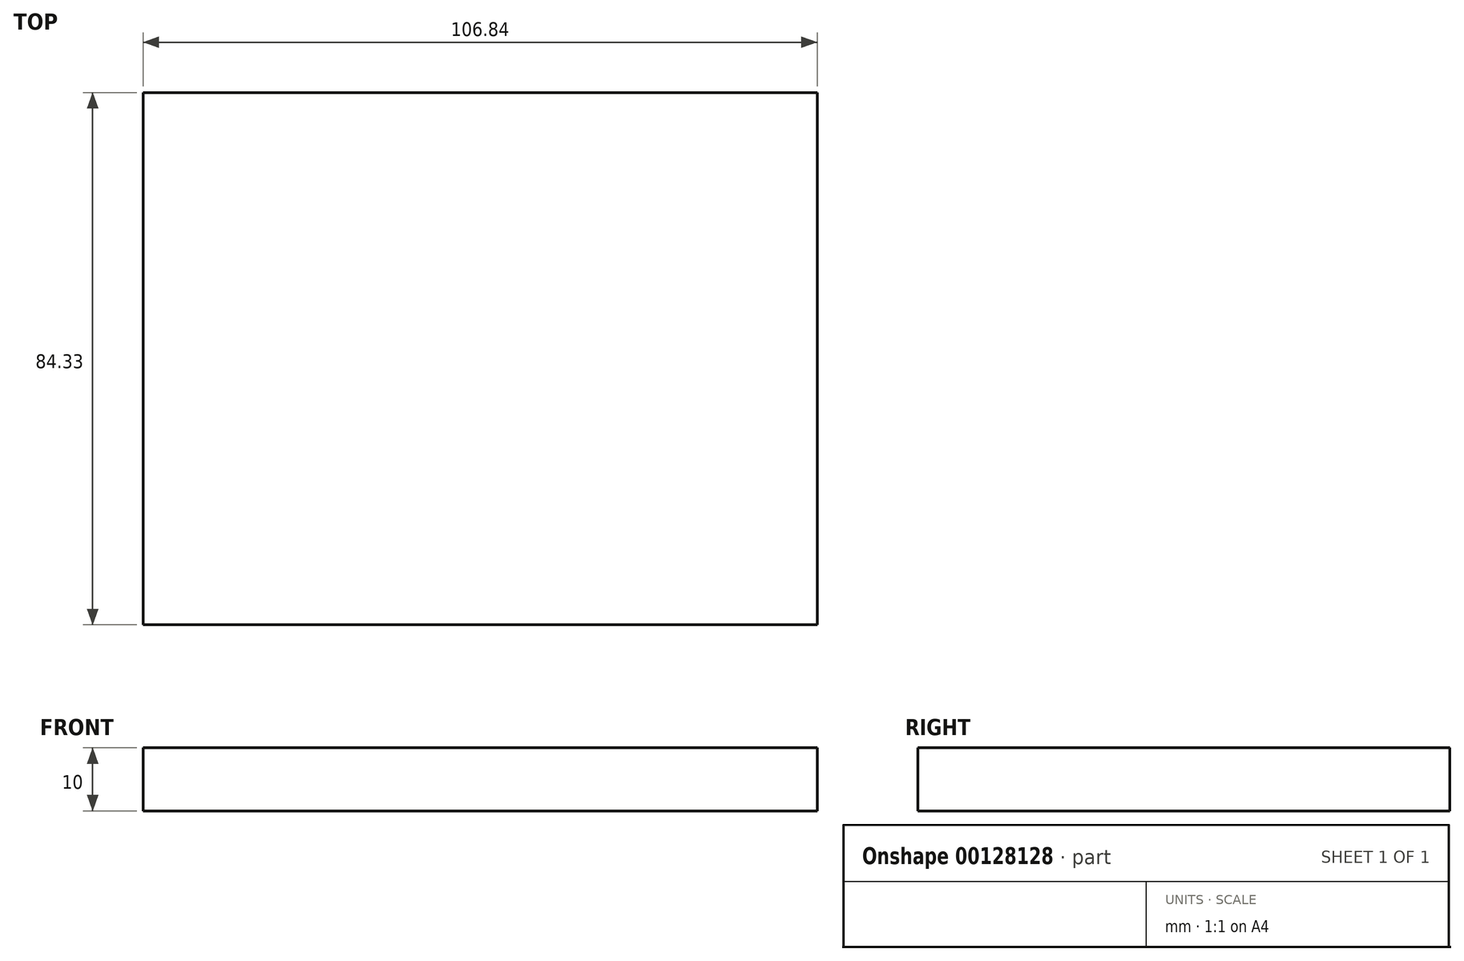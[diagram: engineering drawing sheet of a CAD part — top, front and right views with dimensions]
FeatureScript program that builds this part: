
annotation { "Feature Type Name" : "Feature", "Feature Type Description" : "" }
export const myFeature = defineFeature(function(context is Context, id is Id, definition is map)
    precondition{}
    {
        {
            var Q0;
            Q0=qCreatedBy(makeId("Top.planeOp"),FACE);
            var sketch = newSketch(context, id + "F0", { "sketchPlane" : qUnion([Q0])});
            skLineSegment(sketch, "E0.bottom", {"start": v(0, 0) * mm, "end": v(106.84, 0) * mm});
            skLineSegment(sketch, "E0.top", {"start": v(0, 84.33) * mm, "end": v(106.84, 84.33) * mm});
            skLineSegment(sketch, "E0.left", {"start": v(0, 0) * mm, "end": v(0, 84.33) * mm});
            skLineSegment(sketch, "E0.right", {"start": v(106.84, 0) * mm, "end": v(106.84, 84.33) * mm});
            skSolve(sketch);
        }
        {
            var Q0;
            Q0 = qSketchRegion(id + "F0", true);
            extrude(context, id + "F1", {"entities" : qUnion([Q0]), "depth" : 10 * mm});
        }
    });
